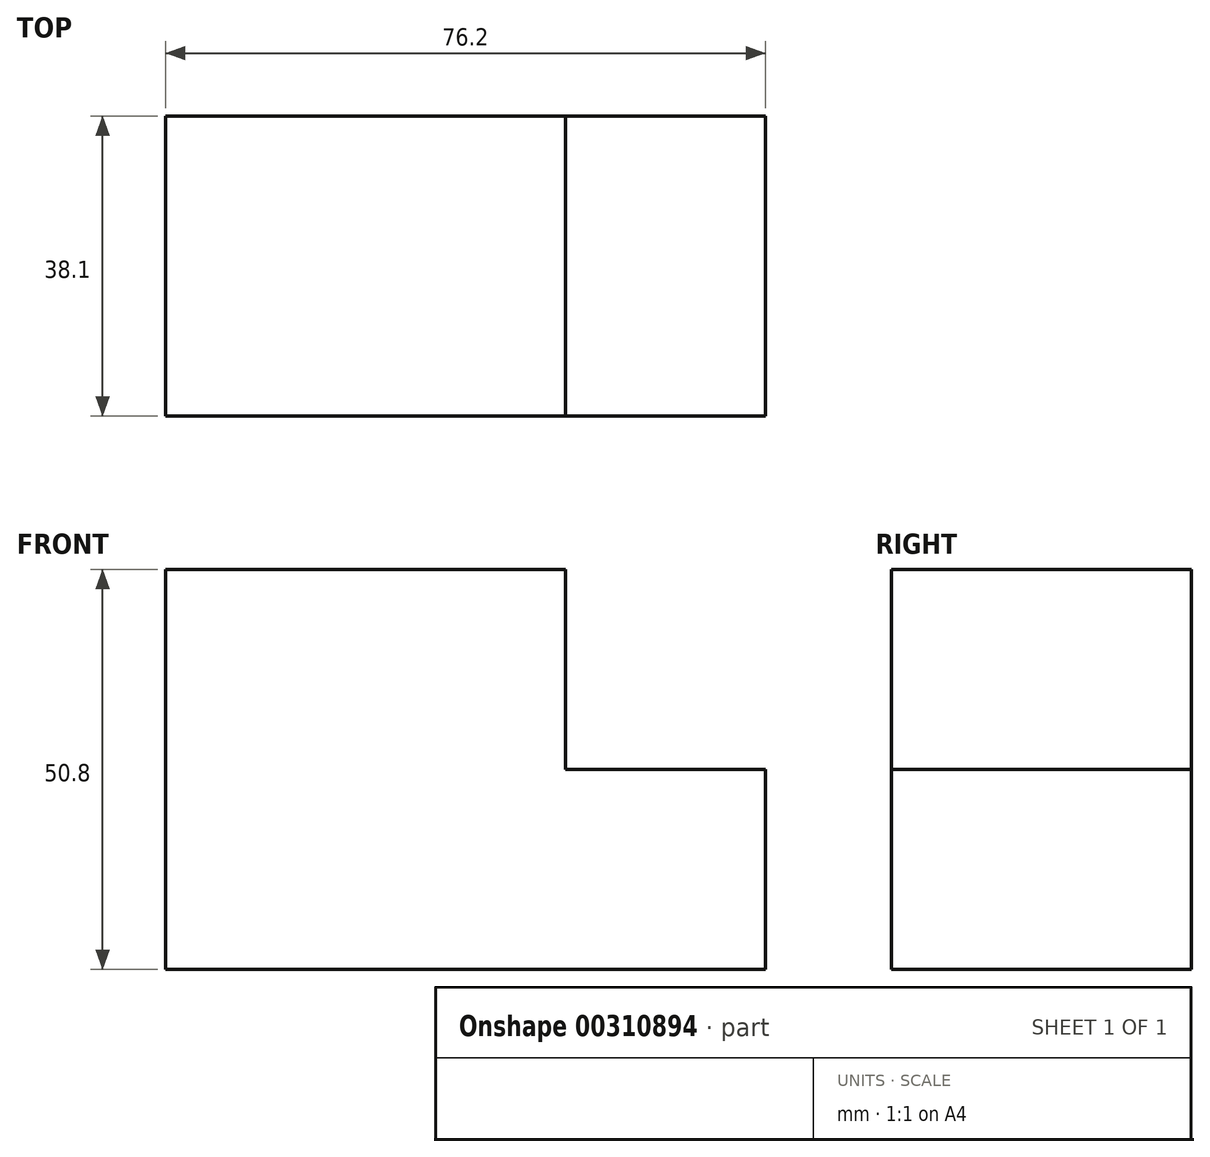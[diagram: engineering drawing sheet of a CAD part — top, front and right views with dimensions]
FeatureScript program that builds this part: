
annotation { "Feature Type Name" : "Feature", "Feature Type Description" : "" }
export const myFeature = defineFeature(function(context is Context, id is Id, definition is map)
    precondition{}
    {
        {
            var Q0;
            Q0=qCreatedBy(makeId("Front.planeOp"),FACE);
            var sketch = newSketch(context, id + "F0", { "sketchPlane" : qUnion([Q0])});
            skLineSegment(sketch, "E0", {"start": v(-44.26, -45.62) * mm, "end": v(31.94, -45.62) * mm});
            skLineSegment(sketch, "E1", {"start": v(31.94, -45.62) * mm, "end": v(31.94, -20.22) * mm});
            skLineSegment(sketch, "E2", {"start": v(31.94, -20.22) * mm, "end": v(6.54, -20.22) * mm});
            skLineSegment(sketch, "E3", {"start": v(6.54, -20.22) * mm, "end": v(6.54, 5.18) * mm});
            skLineSegment(sketch, "E4", {"start": v(6.54, 5.18) * mm, "end": v(-44.26, 5.18) * mm});
            skLineSegment(sketch, "E5", {"start": v(-44.26, 5.18) * mm, "end": v(-44.26, -45.62) * mm});
            skSolve(sketch);
        }
        {
            var Q0;
            Q0=makeQuery(id+"F0.imprint","IMPRINT",FACE,{"disambiguationData":[TD([[makeQuery(id+"F0.imprint","IMPRINT",EDGE,{"derivedFrom":sQuery(id+"F0.wireOp",EDGE,"E0")}),1.0]])]});
            extrude(context, id + "F1", {"entities" : qUnion([Q0]), "depth" : 38.1 * mm});
        }
    });
